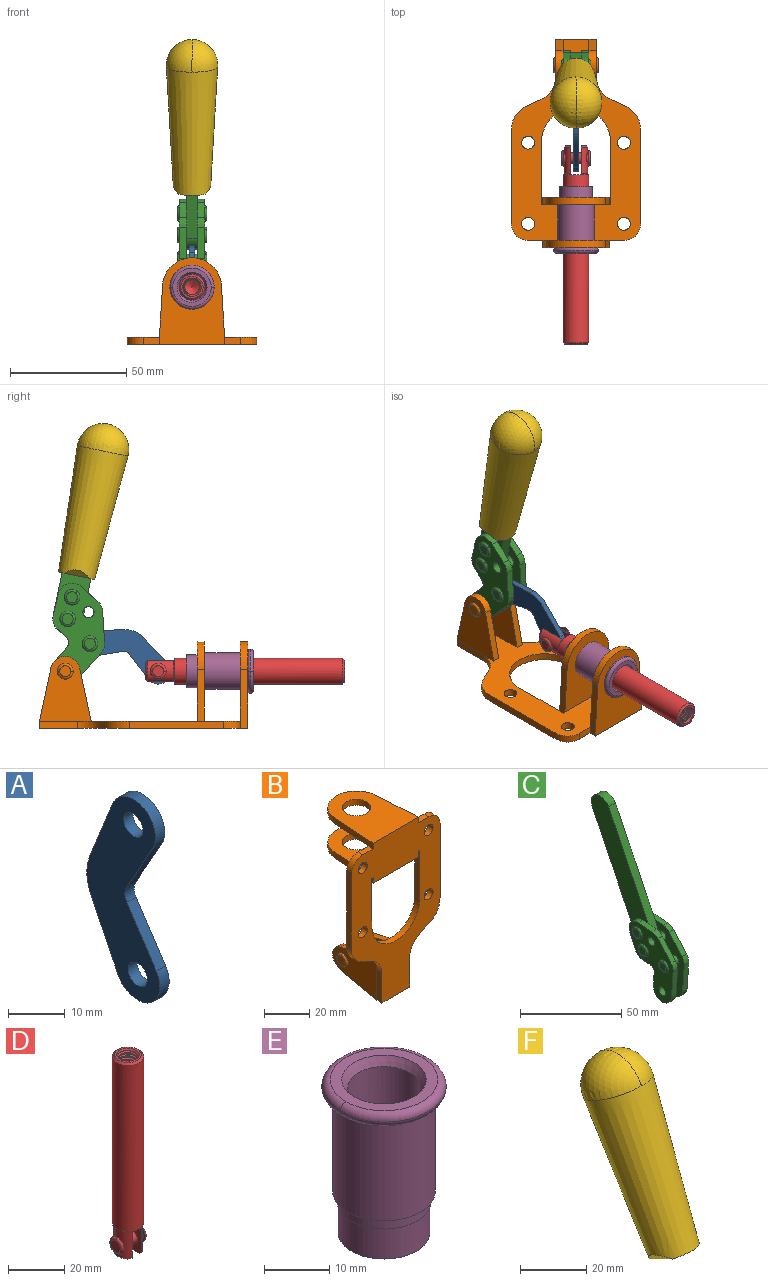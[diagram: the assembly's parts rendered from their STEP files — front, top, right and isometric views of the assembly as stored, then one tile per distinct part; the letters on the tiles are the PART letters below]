
ASSEMBLY  parts=6 mates=6
PART A: 12 faces, bbox 2.3x18.2x42.8 mm
  f0: cylinder r=2.4mm len=4.8mm, axis (1,0,0), area 34.9mm2, adj f4,f11
  f1: cylinder r=10.41mm len=8.47mm, axis (1,0,0), area 20.2mm2, adj f4,f9,f10,f11
  f2: cylinder r=3.05mm len=3.16mm, axis (1,0,0), area 7.7mm2, adj f4,f6,f7,f11
  f3: cylinder r=2.4mm len=4.8mm, axis (1,0,0), area 34.9mm2, adj f4,f11
  f4: plane 42.81x18.23mm, normal (-1,0,0), area 414.1mm2, adj f0,f1,f2,f3,f5,f6,f7,f8
  f5: cylinder r=5.54mm len=10.67mm, axis (1,0,0), area 41.8mm2, adj f4,f6,f10,f11
  f6: plane 11.66x6.53mm, normal (0,-0.87,-0.49), area 30.9mm2, adj f2,f4,f5,f11
  f7: plane 11.17x7.33mm, normal (0,-0.84,0.55), area 30.9mm2, adj f2,f4,f8,f11
  f8: cylinder r=5.54mm len=10.51mm, axis (1,0,0), area 41.8mm2, adj f4,f7,f9,f11
  f9: plane 13.67x6.67mm, normal (0,0.9,-0.44), area 35.1mm2, adj f1,f4,f8,f11
  f10: plane 14.1x5.7mm, normal (0,0.93,0.37), area 35.1mm2, adj f1,f4,f5,f11
  f11: plane 42.81x18.23mm, normal (1,0,0), area 414.1mm2, adj f0,f1,f2,f3,f5,f6,f7,f8
PART B: 55 faces, bbox 55.7x37.4x89.8 mm
  f0: torus R=2.41mm, axis (-1,0,0), area 15mm2, adj f11,f15,f25
  f1: torus R=2.41mm, axis (-1,0,0), area 15mm2, adj f10,f12,f22
  f2: cylinder r=2.78mm len=5.56mm, axis (0,-1,0), area 54.2mm2, adj f30,f54
  f3: cylinder r=14.99mm len=29.97mm, axis (0,-1,0), area 145.9mm2, adj f30,f49,f53,f54
  f4: cylinder r=2.78mm len=5.56mm, axis (0,-1,0), area 54.2mm2, adj f30,f54
  f5: cylinder r=2.78mm len=5.56mm, axis (0,-1,0), area 54.2mm2, adj f30,f54
  f6: cylinder r=2.78mm len=5.56mm, axis (0,-1,0), area 54.2mm2, adj f30,f54
  f7: cylinder r=6.35mm len=12.7mm, axis (0,0,1), area 123.6mm2, adj f27,f51
  f8: cylinder r=6.35mm len=12.7mm, axis (0,0,-1), area 124.7mm2, adj f21,f35
  f9: cylinder r=2.41mm len=11.18mm, axis (-1,0,0), area 169.4mm2, adj f16,f19
  f10: plane 4.83x4.83mm, normal (1,0,0), area 18.3mm2, adj f1,f12
  f11: plane 4.83x4.83mm, normal (-1,0,0), area 18.3mm2, adj f0,f15
  f12: torus R=2.41mm, axis (-1,0,0), area 15mm2, adj f1,f10,f22
  f13: cylinder r=6.35mm len=12.41mm, axis (1,0,0), area 53.4mm2, adj f18,f19,f22,f23
  f14: cylinder r=6.35mm len=12.41mm, axis (-1,0,0), area 53.4mm2, adj f16,f17,f24,f25
  f15: torus R=2.41mm, axis (-1,0,0), area 15mm2, adj f0,f11,f25
  f16: plane 27.86x22.35mm, normal (1,0,0), area 425.4mm2, adj f9,f14,f17,f24,f30
  f17: plane 22.86x4.97mm, normal (0,0.21,0.98), area 72.5mm2, adj f14,f16,f25,f30
  f18: plane 22.86x4.97mm, normal (0,0.21,0.98), area 72.5mm2, adj f13,f19,f22,f30
  f19: plane 27.86x22.35mm, normal (-1,0,0), area 425.4mm2, adj f9,f13,f18,f23,f30
  f20: cylinder r=12.7mm len=25.35mm, axis (0,0,-1), area 119.8mm2, adj f21,f34,f35,f36
  f21: plane 34.21x28.07mm, normal (0,0,-1), area 702.4mm2, adj f8,f20,f30,f34,f36
  f22: plane 27.96x22.45mm, normal (1,0,0), area 407.2mm2, adj f1,f12,f13,f18,f23,f30,f42,f43
  f23: plane 22.86x4.97mm, normal (0,0.21,-0.98), area 72.5mm2, adj f13,f19,f22,f44
  f24: plane 22.86x4.97mm, normal (0,0.21,-0.98), area 72.5mm2, adj f14,f16,f25,f44
  f25: plane 27.86x22.35mm, normal (-1,0,0), area 407.1mm2, adj f0,f14,f15,f17,f24,f30,f45,f46
  f26: plane 3.1x0.95mm, normal (0,0,-1), area 2.7mm2, adj f30,f49,f50,f54
  f27: plane 34.21x28.07mm, normal (0,0,1), area 702.4mm2, adj f7,f28,f30,f50,f52
  f28: cylinder r=12.7mm len=25.35mm, axis (0,0,1), area 118.8mm2, adj f27,f50,f51,f52
  f29: plane 3.1x0.95mm, normal (0,0,-1), area 2.7mm2, adj f30,f52,f53,f54
  f30: plane 86.54x55.63mm, normal (0,1,0), area 2362.9mm2, adj f2,f3,f4,f5,f6,f16,f17,f18
  f31: plane 40.56x3.1mm, normal (-1,0,0), area 125.7mm2, adj f30,f32,f48,f54
  f32: cylinder r=7.11mm len=7.11mm, axis (0,-1,0), area 34.6mm2, adj f30,f31,f33,f54
  f33: plane 6.67x3.1mm, normal (0,0,1), area 20.4mm2, adj f30,f32,f34,f54
  f34: plane 25.39x3.13mm, normal (-1,0.06,0), area 79.5mm2, adj f20,f21,f33,f35,f54
  f35: plane 37.31x28.45mm, normal (0,0,1), area 789.9mm2, adj f8,f20,f34,f36,f54
  f36: plane 25.39x3.13mm, normal (1,0.06,0), area 79.5mm2, adj f20,f21,f35,f37,f54
  f37: plane 6.67x3.1mm, normal (0,0,1), area 20.4mm2, adj f30,f36,f38,f54
  f38: cylinder r=7.11mm len=7.11mm, axis (0,-1,0), area 34.6mm2, adj f30,f37,f39,f54
  f39: plane 40.56x3.1mm, normal (1,0,0), area 125.7mm2, adj f30,f38,f40,f54
  f40: cylinder r=11.18mm len=10.16mm, axis (0,-1,0), area 39.5mm2, adj f30,f39,f41,f54
  f41: plane 6.09x3.1mm, normal (0.42,0,-0.91), area 20.8mm2, adj f30,f40,f42,f54
  f42: cylinder r=11.18mm len=9.41mm, axis (0,-1,0), area 37.2mm2, adj f22,f30,f41,f43,f54
  f43: plane 16.5x3.1mm, normal (1,0,0), area 51.1mm2, adj f22,f42,f44,f54
  f44: plane 17.37x3.1mm, normal (0,0,-1), area 53.8mm2, adj f23,f24,f30,f43,f45,f54
  f45: plane 16.5x3.1mm, normal (-1,0,0), area 51.1mm2, adj f25,f44,f46,f54
  f46: cylinder r=11.18mm len=9.41mm, axis (0,-1,0), area 37.2mm2, adj f25,f30,f45,f47,f54
  f47: plane 6.09x3.1mm, normal (-0.42,0,-0.91), area 20.8mm2, adj f30,f46,f48,f54
  f48: cylinder r=11.18mm len=10.16mm, axis (0,-1,0), area 39.5mm2, adj f30,f31,f47,f54
  f49: plane 26.54x3.1mm, normal (-1,0,0), area 82.3mm2, adj f3,f26,f30,f54
  f50: plane 25.39x3.1mm, normal (1,0.06,0), area 78.8mm2, adj f26,f27,f28,f51,f54
  f51: plane 37.31x28.45mm, normal (0,0,-1), area 789.9mm2, adj f7,f28,f50,f52,f54
  f52: plane 25.39x3.1mm, normal (-1,0.06,0), area 78.8mm2, adj f27,f28,f29,f51,f54
  f53: plane 26.54x3.1mm, normal (1,0,0), area 82.3mm2, adj f3,f29,f30,f54
  f54: plane 89.66x55.63mm, normal (0,-1,0), area 2678.5mm2, adj f2,f3,f4,f5,f6,f26,f29,f31
PART C: 59 faces, bbox 12.9x60.2x99.6 mm
  f0: torus R=2.39mm, axis (-1,0,0), area 14.9mm2, adj f20,f43,f51
  f1: torus R=2.39mm, axis (-1,0,0), area 14.9mm2, adj f19,f42,f51
  f2: torus R=2.39mm, axis (-1,0,0), area 14.9mm2, adj f18,f35,f51
  f3: torus R=2.39mm, axis (-1,0,0), area 14.9mm2, adj f14,f17,f23
  f4: torus R=2.39mm, axis (-1,0,0), area 14.9mm2, adj f13,f16,f23
  f5: torus R=2.39mm, axis (-1,0,0), area 14.9mm2, adj f12,f15,f23
  f6: cylinder r=2.39mm len=4.78mm, axis (1,0,0), area 46.5mm2, adj f48,f50,f51
  f7: cylinder r=2.39mm len=4.78mm, axis (1,0,0), area 46.5mm2, adj f50,f51
  f8: cylinder r=6.35mm len=12.68mm, axis (1,0,0), area 61.8mm2, adj f38,f39,f50,f51
  f9: cylinder r=2.39mm len=4.78mm, axis (-1,0,0), area 70.5mm2, adj f46,f50
  f10: cylinder r=2.39mm len=4.78mm, axis (-1,0,0), area 46.5mm2, adj f23,f45,f46
  f11: cylinder r=2.39mm len=4.78mm, axis (-1,0,0), area 46.5mm2, adj f23,f46
  f12: plane 4.78x4.78mm, normal (1,0,0), area 17.9mm2, adj f5,f15
  f13: plane 4.78x4.78mm, normal (1,0,0), area 17.9mm2, adj f4,f16
  f14: plane 4.78x4.78mm, normal (1,0,0), area 17.9mm2, adj f3,f17
  f15: torus R=2.39mm, axis (-1,0,0), area 14.9mm2, adj f5,f12,f23
  f16: torus R=2.39mm, axis (-1,0,0), area 14.9mm2, adj f4,f13,f23
  f17: torus R=2.39mm, axis (-1,0,0), area 14.9mm2, adj f3,f14,f23
  f18: plane 4.78x4.78mm, normal (-1,0,0), area 17.9mm2, adj f2,f35
  f19: plane 4.78x4.78mm, normal (-1,0,0), area 17.9mm2, adj f1,f42
  f20: plane 4.78x4.78mm, normal (-1,0,0), area 17.9mm2, adj f0,f43
  f21: plane 2.26x0.2mm, normal (1,0,0), area 0.2mm2, adj f31,f44
  f22: plane 2.26x0.2mm, normal (-1,0,0), area 0.2mm2, adj f41,f44
  f23: plane 39.37x30.77mm, normal (1,0,0), area 565.5mm2, adj f3,f4,f5,f10,f11,f15,f16,f17
  f24: cylinder r=6.1mm len=4.15mm, axis (-1,0,0), area 14.7mm2, adj f23,f25,f32,f46
  f25: plane 10.25x9.01mm, normal (0,-0.75,0.66), area 42.3mm2, adj f23,f24,f26,f46
  f26: cylinder r=6.35mm len=4.64mm, axis (-1,0,0), area 15.6mm2, adj f23,f25,f27,f46
  f27: plane 15.84x3.1mm, normal (0,-1,-0.07), area 49.2mm2, adj f23,f26,f28,f46
  f28: cylinder r=6.35mm len=12.68mm, axis (-1,0,0), area 61.8mm2, adj f23,f27,f29,f46
  f29: plane 8.11x3.1mm, normal (0,1,0.07), area 25.2mm2, adj f23,f28,f30,f46
  f30: cylinder r=3.05mm len=3.25mm, axis (-1,0,0), area 14.8mm2, adj f23,f29,f31,f46
  f31: plane 5.99x3.1mm, normal (0,0.07,-1), area 18.6mm2, adj f21,f23,f30,f44,f46
  f32: plane 9.5x3.1mm, normal (0,-0.07,1), area 29.5mm2, adj f23,f24,f33,f46,f47
  f33: cylinder r=6.1mm len=8.63mm, axis (-1,0,0), area 39.1mm2, adj f23,f32,f34,f47
  f34: plane 8.65x3.96mm, normal (0,0.91,-0.42), area 29.5mm2, adj f23,f33,f44,f47
  f35: torus R=2.39mm, axis (-1,0,0), area 14.9mm2, adj f2,f18,f51
  f36: plane 10.25x9.01mm, normal (0,-0.75,0.66), area 42.3mm2, adj f37,f49,f50,f51
  f37: cylinder r=6.35mm len=4.64mm, axis (1,0,0), area 15.6mm2, adj f36,f38,f50,f51
  f38: plane 15.84x3.1mm, normal (0,-1,-0.07), area 49.2mm2, adj f8,f37,f50,f51
  f39: plane 8.11x3.1mm, normal (0,1,0.07), area 25.2mm2, adj f8,f40,f50,f51
  f40: cylinder r=3.05mm len=3.25mm, axis (1,0,0), area 14.8mm2, adj f39,f41,f50,f51
  f41: plane 5.99x3.1mm, normal (0,0.07,-1), area 18.6mm2, adj f22,f40,f44,f50,f51
  f42: torus R=2.39mm, axis (-1,0,0), area 14.9mm2, adj f1,f19,f51
  f43: torus R=2.39mm, axis (-1,0,0), area 14.9mm2, adj f0,f20,f51
  f44: cylinder r=6.35mm len=12.12mm, axis (-1,0,0), area 128.9mm2, adj f21,f22,f23,f31,f34,f41,f46,f47
  f45: plane 2.65x1.35mm, normal (1,0,0), area 1mm2, adj f10,f55
  f46: plane 39.08x20.42mm, normal (-1,0,0), area 412.5mm2, adj f9,f10,f11,f24,f25,f26,f27,f28
  f47: plane 77.62x39.82mm, normal (1,0,0), area 850mm2, adj f32,f33,f34,f44,f53,f54,f55
  f48: plane 2.65x1.35mm, normal (-1,0,0), area 1mm2, adj f6,f55
  f49: cylinder r=6.1mm len=4.15mm, axis (1,0,0), area 14.7mm2, adj f36,f50,f51,f56
  f50: plane 39.08x20.42mm, normal (1,0,0), area 412.5mm2, adj f6,f7,f8,f9,f36,f37,f38,f39
  f51: plane 39.37x30.77mm, normal (-1,0,0), area 565.5mm2, adj f0,f1,f2,f6,f7,f8,f35,f36
  f52: plane 8.65x3.96mm, normal (0,0.91,-0.42), area 29.5mm2, adj f44,f51,f57,f58
  f53: plane 68.49x33.4mm, normal (0,0.9,-0.44), area 358.1mm2, adj f44,f47,f54,f58
  f54: cylinder r=6.35mm len=12.06mm, axis (1,0,0), area 93.7mm2, adj f47,f53,f55,f58
  f55: plane 68.49x33.4mm, normal (0,-0.9,0.44), area 358.1mm2, adj f44,f45,f46,f47,f48,f50,f54,f58
  f56: plane 9.5x3.1mm, normal (0,-0.07,1), area 29.5mm2, adj f49,f50,f51,f57,f58
  f57: cylinder r=6.1mm len=8.63mm, axis (1,0,0), area 39.1mm2, adj f51,f52,f56,f58
  f58: plane 77.62x39.82mm, normal (-1,0,0), area 850mm2, adj f44,f52,f53,f54,f55,f56,f57
PART D: 48 faces, bbox 12.6x11.1x86.1 mm
  f0: torus R=2.41mm, axis (-1,0,0), area 15mm2, adj f30,f32,f34
  f1: torus R=2.41mm, axis (-1,0,0), area 15mm2, adj f29,f31,f33
  f2: cylinder r=5.54mm len=72.39mm, axis (0,0,1), area 2518.5mm2, adj f3,f4,f42,f43
  f3: cone r=5.54mm half-angle=45deg, axis (0,0,1), area 7.6mm2, adj f2,f5,f41
  f4: cone r=5.54mm half-angle=45deg, axis (0,0,-1), area 34.9mm2, adj f2,f39
  f5: cylinder r=5.08mm len=11.48mm, axis (0,0,1), area 108.3mm2, adj f3,f7,f8,f41
  f6: cylinder r=2.41mm len=4.83mm, axis (-1,0,0), area 71.2mm2, adj f40,f41
  f7: cylinder r=2.41mm len=4.83mm, axis (-1,0,0), area 7.6mm2, adj f5,f34
  f8: cone r=5.08mm half-angle=45deg, axis (0,0,1), area 10.6mm2, adj f5,f37,f41
  f9: cone r=3.98mm half-angle=45deg, axis (0,0,1), area 17.6mm2, adj f27,f39,f45,f46,f47
  f10: cylinder r=2.41mm len=4.83mm, axis (-1,0,0), area 7.6mm2, adj f33,f38
  f11: cylinder r=3.2mm len=6.4mm, axis (0,0,1), area 78.4mm2, adj f12,f28,f44,f45,f47
  f12: cylinder r=3.2mm len=6.4mm, axis (0,0,1), area 10.5mm2, adj f11,f13,f45,f47
  f13: cylinder r=3.2mm len=6.4mm, axis (0,0,1), area 10.5mm2, adj f12,f14,f45,f47
  f14: cylinder r=3.2mm len=6.4mm, axis (0,0,1), area 10.5mm2, adj f13,f15,f45,f47
  f15: cylinder r=3.2mm len=6.4mm, axis (0,0,1), area 10.5mm2, adj f14,f16,f45,f47
  f16: cylinder r=3.2mm len=6.4mm, axis (0,0,1), area 10.5mm2, adj f15,f17,f45,f47
  f17: cylinder r=3.2mm len=6.4mm, axis (0,0,1), area 10.5mm2, adj f16,f18,f45,f47
  f18: cylinder r=3.2mm len=6.4mm, axis (0,0,1), area 10.5mm2, adj f17,f19,f45,f47
  f19: cylinder r=3.2mm len=6.4mm, axis (0,0,1), area 10.5mm2, adj f18,f20,f45,f47
  f20: cylinder r=3.2mm len=6.4mm, axis (0,0,1), area 10.5mm2, adj f19,f21,f45,f47
  f21: cylinder r=3.2mm len=6.4mm, axis (0,0,1), area 10.5mm2, adj f20,f22,f45,f47
  f22: cylinder r=3.2mm len=6.4mm, axis (0,0,1), area 10.5mm2, adj f21,f23,f45,f47
  f23: cylinder r=3.2mm len=6.4mm, axis (0,0,1), area 10.5mm2, adj f22,f24,f45,f47
  f24: cylinder r=3.2mm len=6.4mm, axis (0,0,1), area 10.5mm2, adj f23,f25,f45,f47
  f25: cylinder r=3.2mm len=6.4mm, axis (0,0,1), area 10.5mm2, adj f24,f26,f45,f47
  f26: cylinder r=3.2mm len=6.4mm, axis (0,0,1), area 10.5mm2, adj f25,f27,f45,f47
  f27: cylinder r=3.2mm len=6.4mm, axis (0,0,1), area 7.4mm2, adj f9,f26,f45,f47
  f28: cone r=3.2mm half-angle=60deg, axis (0,0,1), area 37.2mm2, adj f11
  f29: plane 4.83x4.83mm, normal (-1,0,0), area 18.3mm2, adj f1,f31
  f30: plane 4.83x4.83mm, normal (1,0,0), area 18.3mm2, adj f0,f32
  f31: torus R=2.41mm, axis (-1,0,0), area 15mm2, adj f1,f29,f33
  f32: torus R=2.41mm, axis (-1,0,0), area 15mm2, adj f0,f30,f34
  f33: plane 6.83x6.83mm, normal (1,0,0), area 18.3mm2, adj f1,f10,f31
  f34: plane 6.83x6.83mm, normal (-1,0,0), area 18.3mm2, adj f0,f7,f32
  f35: cone r=5.08mm half-angle=45deg, axis (0,0,1), area 10.6mm2, adj f36,f38,f40
  f36: plane 7.25x1.97mm, normal (0,0,-1), area 10mm2, adj f35,f40
  f37: plane 7.25x1.97mm, normal (0,0,-1), area 10mm2, adj f8,f41
  f38: cylinder r=5.08mm len=11.48mm, axis (0,0,1), area 108.3mm2, adj f10,f35,f40,f42
  f39: plane 9.55x9.55mm, normal (0,0,1), area 22mm2, adj f4,f9
  f40: plane 12.76x10.09mm, normal (1,0,0), area 95.7mm2, adj f6,f35,f36,f38,f42,f43
  f41: plane 12.76x10.09mm, normal (-1,0,0), area 95.7mm2, adj f3,f5,f6,f8,f37,f43
  f42: cone r=5.54mm half-angle=45deg, axis (0,0,1), area 7.6mm2, adj f2,f38,f40
  f43: plane 11.07x4.7mm, normal (0,0,-1), area 50.4mm2, adj f2,f40,f41
  f44: plane 0.89x0.62mm, normal (-1,0,0), area 0.3mm2, adj f11,f45,f46,f47
  f45: bspline ~24.8x7.63mm, area 266.6mm2, adj f9,f11,f12,f13,f14,f15,f16,f17
  f46: bspline ~24.87x7.63mm, area 73.6mm2, adj f9,f44,f45,f47
  f47: bspline ~24.98x7.63mm, area 272.5mm2, adj f9,f11,f12,f13,f14,f15,f16,f17
PART E: 15 faces, bbox 20.6x20.6x28.7 mm
  f0: torus R=8.26mm, axis (0,0,1), area 56.8mm2, adj f1,f10,f12
  f1: torus R=8.26mm, axis (0,0,1), area 56.8mm2, adj f0,f6,f13
  f2: cylinder r=5.59mm len=25.91mm, axis (0,0,1), area 909.6mm2, adj f3,f4
  f3: cone r=6.86mm half-angle=45deg, axis (0,0,-1), area 70.2mm2, adj f2,f14
  f4: cone r=6.47mm half-angle=30deg, axis (0,0,1), area 66.7mm2, adj f2,f13
  f5: cylinder r=7.04mm len=14.07mm, axis (0,0,1), area 252.6mm2, adj f11,f14
  f6: torus R=8.26mm, axis (0,0,1), area 56.8mm2, adj f1,f12,f13
  f7: cylinder r=7.16mm len=14.33mm, axis (0,0,1), area 91.5mm2, adj f9,f11
  f8: cylinder r=7.86mm len=18.42mm, axis (0,0,1), area 909.6mm2, adj f9,f10
  f9: plane 15.72x15.72mm, normal (0,0,-1), area 33mm2, adj f7,f8
  f10: plane 16.51x16.51mm, normal (0,0,-1), area 19.9mm2, adj f0,f8,f12
  f11: plane 14.33x14.33mm, normal (0,0,-1), area 5.7mm2, adj f5,f7
  f12: torus R=8.26mm, axis (0,0,1), area 56.8mm2, adj f0,f6,f10
  f13: plane 16.51x16.51mm, normal (0,0,1), area 82.7mm2, adj f1,f4,f6
  f14: plane 14.07x14.07mm, normal (0,0,-1), area 7.8mm2, adj f3,f5
PART F: 11 faces, bbox 22.3x42.6x64.5 mm
  f0: sphere r=11.13mm, area 411.4mm2, adj f1,f8
  f1: cone r=11.11mm half-angle=3.3deg, axis (0,0.44,0.9), area 3251.8mm2, adj f0,f7,f8,f9,f10
  f2: cylinder r=6.16mm len=11.7mm, axis (1,0,0), area 89.5mm2, adj f3,f4,f5,f6
  f3: plane 60.23x36.75mm, normal (-1,0,0), area 763.6mm2, adj f2,f4,f6,f10
  f4: plane 51.37x25.05mm, normal (0,0.9,-0.44), area 264.2mm2, adj f2,f3,f5,f10
  f5: plane 60.23x36.75mm, normal (1,0,0), area 763.6mm2, adj f2,f4,f6,f10
  f6: plane 51.37x25.05mm, normal (0,-0.9,0.44), area 264.2mm2, adj f2,f3,f5,f10
  f7: plane 9.95x5.95mm, normal (0.71,-0.31,-0.64), area 25.8mm2, adj f1,f10
  f8: sphere r=11.13mm, area 411.4mm2, adj f0,f1
  f9: plane 9.95x5.95mm, normal (-0.71,-0.31,-0.64), area 25.8mm2, adj f1,f10
  f10: plane 14.27x11.38mm, normal (0,-0.44,-0.9), area 106.7mm2, adj f1,f3,f4,f5,f6,f7,f9
PLACE A rot(axis=(1,0,0),113.9deg) t=(0,25.6,8.37)mm
PLACE B rot(axis=(1,0,0),90deg) t=(0,9.43,0)mm fixed
PLACE C rot(axis=(1,0,0),37.8deg) t=(0,2.41,34.89)mm
PLACE D rot(axis=(1,0,0),90deg) t=(0,16.96,0)mm
PLACE E rot(axis=(1,0,0),90deg) t=(0,9.43,0)mm
PLACE F rot(axis=(1,0,0),37.8deg) t=(0,2.41,34.89)mm
MATE fastened E.f2 <-> B.f7  axis (0,1,0) through (0,-36.96,24.61)mm
MATE revolute D.f6 <-> A.f5  axis (-1,0,0) through (0,1.48,24.61)mm
MATE revolute C.f4 <-> A.f3  axis (-1,0,0) through (0,30.94,36.45)mm
MATE fastened C.f54 <-> F.f2  axis (1,0,0) through (0,24.98,121.71)mm
MATE revolute C.f7 <-> B.f0  axis (-1,0,0) through (0,41.52,24.61)mm
MATE slider D.f2 <-> B.f7  axis (0,-1,0) through (0,-41.83,24.61)mm
